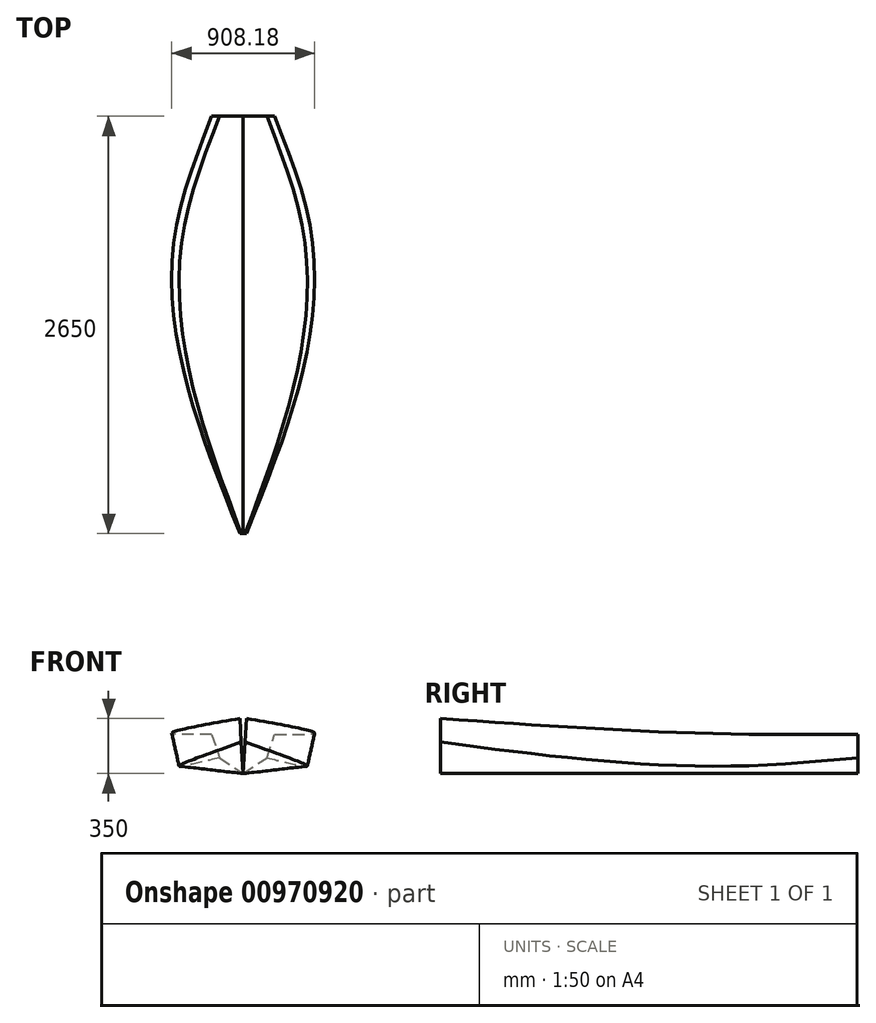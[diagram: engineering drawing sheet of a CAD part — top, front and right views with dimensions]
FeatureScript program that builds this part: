
annotation { "Feature Type Name" : "Feature", "Feature Type Description" : "" }
export const myFeature = defineFeature(function(context is Context, id is Id, definition is map)
    precondition{}
    {
        {
            var Q0;
            Q0=qCreatedBy(makeId("Front.planeOp"),FACE);
            var sketch = newSketch(context, id + "F0", { "sketchPlane" : qUnion([Q0])});
            skLineSegment(sketch, "E0", {"start": v(-425, 250) * mm, "end": v(-375, 50) * mm});
            skLineSegment(sketch, "E1", {"start": v(-375, 50) * mm, "end": v(0, 0) * mm});
            skLineSegment(sketch, "E2", {"start": v(0, 0) * mm, "end": v(375, 50) * mm});
            skLineSegment(sketch, "E3", {"start": v(375, 50) * mm, "end": v(425, 250) * mm});
            skLineSegment(sketch, "E4", {"start": v(0, -126.18) * mm, "end": v(0, 368.5) * mm, "construction": true});
            skSolve(sketch);
        }
        {
            var Q0;
            Q0=qCreatedBy(makeId("Front.planeOp"),FACE);
            cPlane(context, id + "F1", {"entities" : qUnion([Q0]), "cplaneType" : CPlaneType.OFFSET, "offset" : 700 * mm, "oppositeDirection" : true, "width" : 150 * mm, "height" : 150 * mm});
        }
        {
            var Q0;
            Q0=qCreatedBy(id+"F1.planeOp",FACE);
            var sketch = newSketch(context, id + "F2", { "sketchPlane" : qUnion([Q0])});
            skLineSegment(sketch, "E5", {"start": v(-200, 250) * mm, "end": v(-150, 100) * mm});
            skLineSegment(sketch, "E6", {"start": v(-150, 100) * mm, "end": v(0, 0) * mm});
            skLineSegment(sketch, "E7", {"start": v(0, 0) * mm, "end": v(150, 100) * mm});
            skLineSegment(sketch, "E8", {"start": v(150, 100) * mm, "end": v(200, 250) * mm});
            skLineSegment(sketch, "E9", {"start": v(0, -270.38) * mm, "end": v(0, 270.38) * mm, "construction": true});
            skPoint(sketch, "E10.0", {"position": v(0, 0) * mm});
            skSolve(sketch);
        }
        {
            var Q0;
            Q0=qCreatedBy(makeId("Front.planeOp"),FACE);
            cPlane(context, id + "F3", {"entities" : qUnion([Q0]), "cplaneType" : CPlaneType.OFFSET, "offset" : 1950 * mm, "width" : 150 * mm, "height" : 150 * mm});
        }
        {
            var Q0;
            Q0=qCreatedBy(id+"F3.planeOp",FACE);
            var sketch = newSketch(context, id + "F4", { "sketchPlane" : qUnion([Q0])});
            skLineSegment(sketch, "E11", {"start": v(-20, 350) * mm, "end": v(-12.5, 200) * mm});
            skLineSegment(sketch, "E12", {"start": v(-12.5, 200) * mm, "end": v(0, 0) * mm});
            skLineSegment(sketch, "E13", {"start": v(0, 0) * mm, "end": v(12.5, 200) * mm});
            skLineSegment(sketch, "E14", {"start": v(12.5, 200) * mm, "end": v(20, 350) * mm});
            skLineSegment(sketch, "E15", {"start": v(0, -274.27) * mm, "end": v(0, 274.27) * mm, "construction": true});
            skPoint(sketch, "E16.0", {"position": v(0, 0) * mm});
            skSolve(sketch);
        }
        {
            var Q0;
            Q0 = qConstructionFilter(qBodyType(qCreatedBy(id + "F2" ,EDGE), BodyType.WIRE), ConstructionObject.NO);
            var Q1;
            Q1 = qConstructionFilter(qBodyType(qCreatedBy(id + "F0" ,EDGE), BodyType.WIRE), ConstructionObject.NO);
            var Q2;
            Q2 = qConstructionFilter(qBodyType(qCreatedBy(id + "F4" ,EDGE), BodyType.WIRE), ConstructionObject.NO);
            loft(context, id + "F5", {"bodyType" : ToolBodyType.SURFACE, "wireProfilesArray" : [{ "wireProfileEntities" : qUnion([Q0]) }, { "wireProfileEntities" : qUnion([Q1]) }, { "wireProfileEntities" : qUnion([Q2]) }]});
        }
    });
